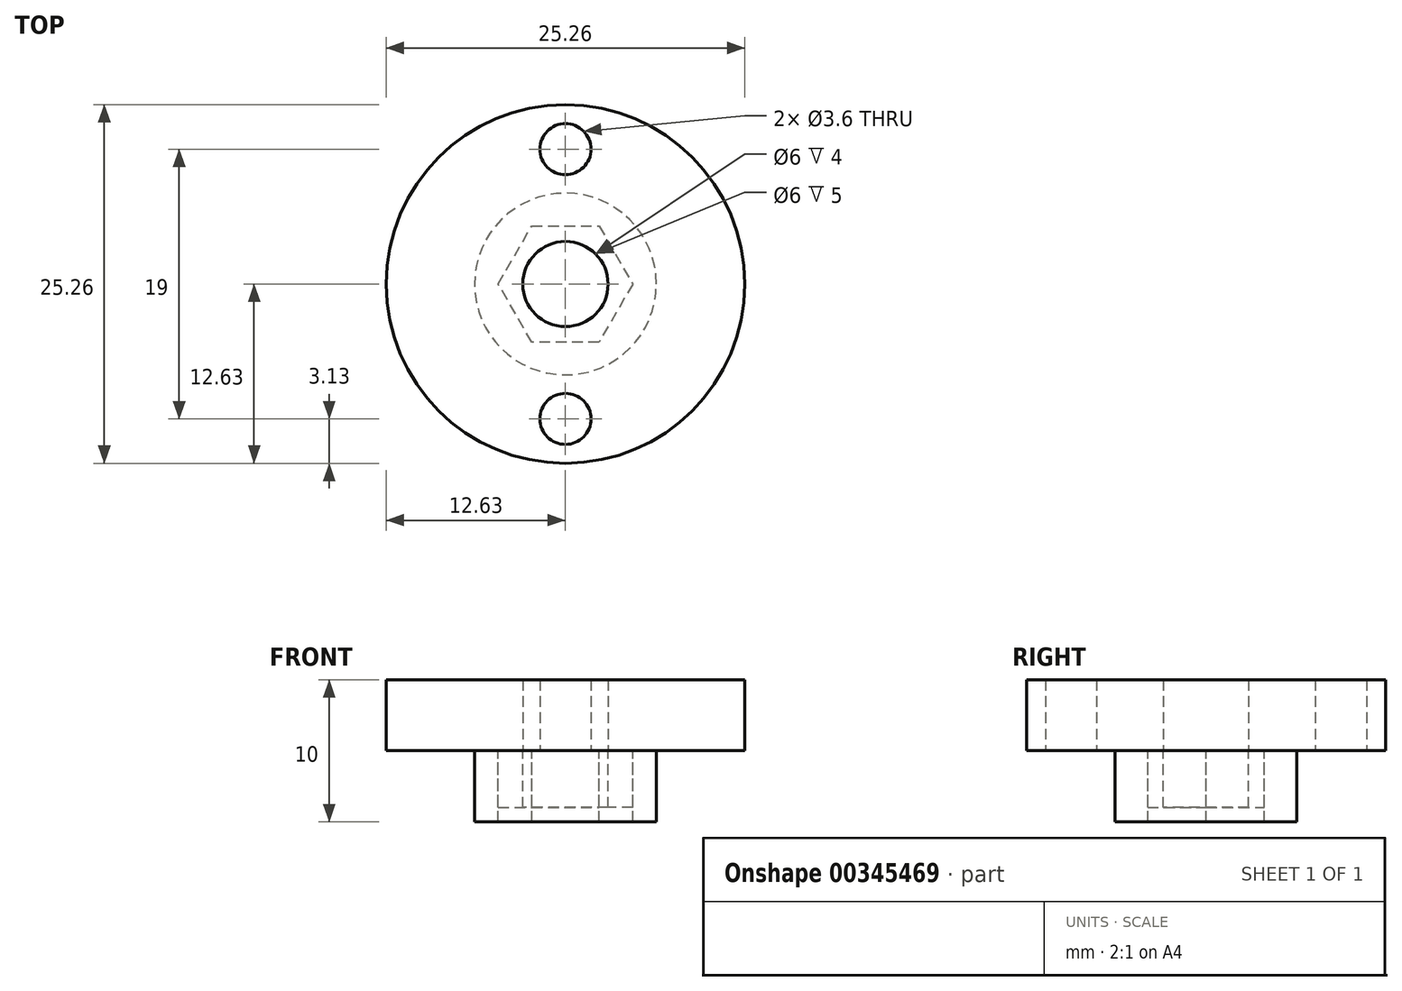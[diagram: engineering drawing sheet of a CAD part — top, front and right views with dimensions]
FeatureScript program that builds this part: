
annotation { "Feature Type Name" : "Feature", "Feature Type Description" : "" }
export const myFeature = defineFeature(function(context is Context, id is Id, definition is map)
    precondition{}
    {
        {
            var Q0;
            Q0=qCreatedBy(makeId("Top.planeOp"),FACE);
            var sketch = newSketch(context, id + "F0", { "sketchPlane" : qUnion([Q0])});
            skCircle(sketch, "E0", {"center": v(0, 0) * mm, "radius": 12.63 * mm});
            skCircle(sketch, "E1", {"center": v(0, 0) * mm, "radius": 6.4 * mm});
            skCircle(sketch, "E2", {"center": v(0, 0) * mm, "radius": 3 * mm});
            skCircle(sketch, "E3.cCircle", {"center": v(0, 0) * mm, "radius": 4.1 * mm, "construction": true});
            skLineSegment(sketch, "E3.0", {"start": v(-2.37, 4.1) * mm, "end": v(2.37, 4.1) * mm});
            skLineSegment(sketch, "E3.1", {"start": v(2.37, 4.1) * mm, "end": v(4.73, 0) * mm});
            skLineSegment(sketch, "E3.2", {"start": v(4.73, 0) * mm, "end": v(2.37, -4.1) * mm});
            skLineSegment(sketch, "E3.3", {"start": v(2.37, -4.1) * mm, "end": v(-2.37, -4.1) * mm});
            skLineSegment(sketch, "E3.4", {"start": v(-2.37, -4.1) * mm, "end": v(-4.73, 0) * mm});
            skLineSegment(sketch, "E3.5", {"start": v(-4.73, 0) * mm, "end": v(-2.37, 4.1) * mm});
            skPoint(sketch, "E3.0.midPoint", {"position": v(0, 4.1) * mm});
            skCircle(sketch, "E4", {"center": v(0, 9.5) * mm, "radius": 1.8 * mm});
            skCircle(sketch, "E5", {"center": v(0, -9.5) * mm, "radius": 1.8 * mm});
            skLineSegment(sketch, "E6", {"start": v(0, 9.5) * mm, "end": v(0, -9.5) * mm, "construction": true});
            skSolve(sketch);
        }
        {
            var Q0;
            Q0=makeQuery(id+"F0.imprint","IMPRINT",FACE,{"disambiguationData":[TD([[makeQuery(id+"F0.imprint","IMPRINT",EDGE,{"derivedFrom":sQuery(id+"F0.wireOp",EDGE,"E0")}),1.0]])]});
            var Q1;
            Q1=makeQuery(id+"F0.imprint","IMPRINT",FACE,{"disambiguationData":[TD([[makeQuery(id+"F0.imprint","IMPRINT",EDGE,{"derivedFrom":sQuery(id+"F0.wireOp",EDGE,"E1")}),1.0]])]});
            var Q2;
            Q2=makeQuery(id+"F0.imprint","IMPRINT",FACE,{"disambiguationData":[TD([[makeQuery(id+"F0.imprint","IMPRINT",EDGE,{"derivedFrom":sQuery(id+"F0.wireOp",EDGE,"E2")}),-1.0]])]});
            extrude(context, id + "F1", {"entities" : qUnion([Q0, Q1, Q2]), "depth" : 5 * mm});
        }
        {
            var Q0;
            Q0=makeQuery(id+"F0.imprint","IMPRINT",FACE,{"disambiguationData":[TD([[makeQuery(id+"F0.imprint","IMPRINT",EDGE,{"derivedFrom":sQuery(id+"F0.wireOp",EDGE,"E1")}),1.0]])]});
            extrude(context, id + "F2", {"entities" : qUnion([Q0]), "operationType" : NewBodyOperationType.ADD, "oppositeDirection" : true, "depth" : 5 * mm});
        }
        {
            var Q0;
            Q0=makeQuery(id+"F0.imprint","IMPRINT",FACE,{"disambiguationData":[TD([[makeQuery(id+"F0.imprint","IMPRINT",EDGE,{"derivedFrom":sQuery(id+"F0.wireOp",EDGE,"E2")}),-1.0]])]});
            extrude(context, id + "F3", {"entities" : qUnion([Q0]), "oppositeDirection" : true, "depth" : 4 * mm});
        }
    });
